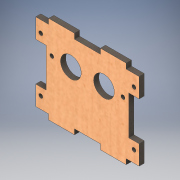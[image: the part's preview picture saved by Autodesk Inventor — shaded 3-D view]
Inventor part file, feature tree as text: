
AUTODESK INVENTOR PART (.ipt)
format: ipt  version: 2019 (Build 230136000, 136)  size: 190,464 bytes
history: native  units: mm
features: sketch x4, hole x3, other x1, extrude x1
ambient origin geometry x8: Origin, YZ Plane, XZ Plane, XY Plane, X Axis, Y Axis, Z Axis, Center Point
bodies: Body1 (feature_tree)
feature tree (9):
  other  "Твердое тело1"
  extrude  "Выдавливание1"  Depth=4.0mm
  hole  "Отверстие1"  [1 undecoded]
  hole  "Отверстие2"  [1 undecoded]
  hole  "Отверстие3"  [1 undecoded]
  sketch  "Эскиз1"
  sketch  "Эскиз2"
  sketch  "Эскиз3"
  sketch  "Эскиз4"
note: 3 required parameter values undecoded (feature->parameter linkage not recoverable at this tier; creation-order binding heuristic only, values carry confidence <= 0.55)
